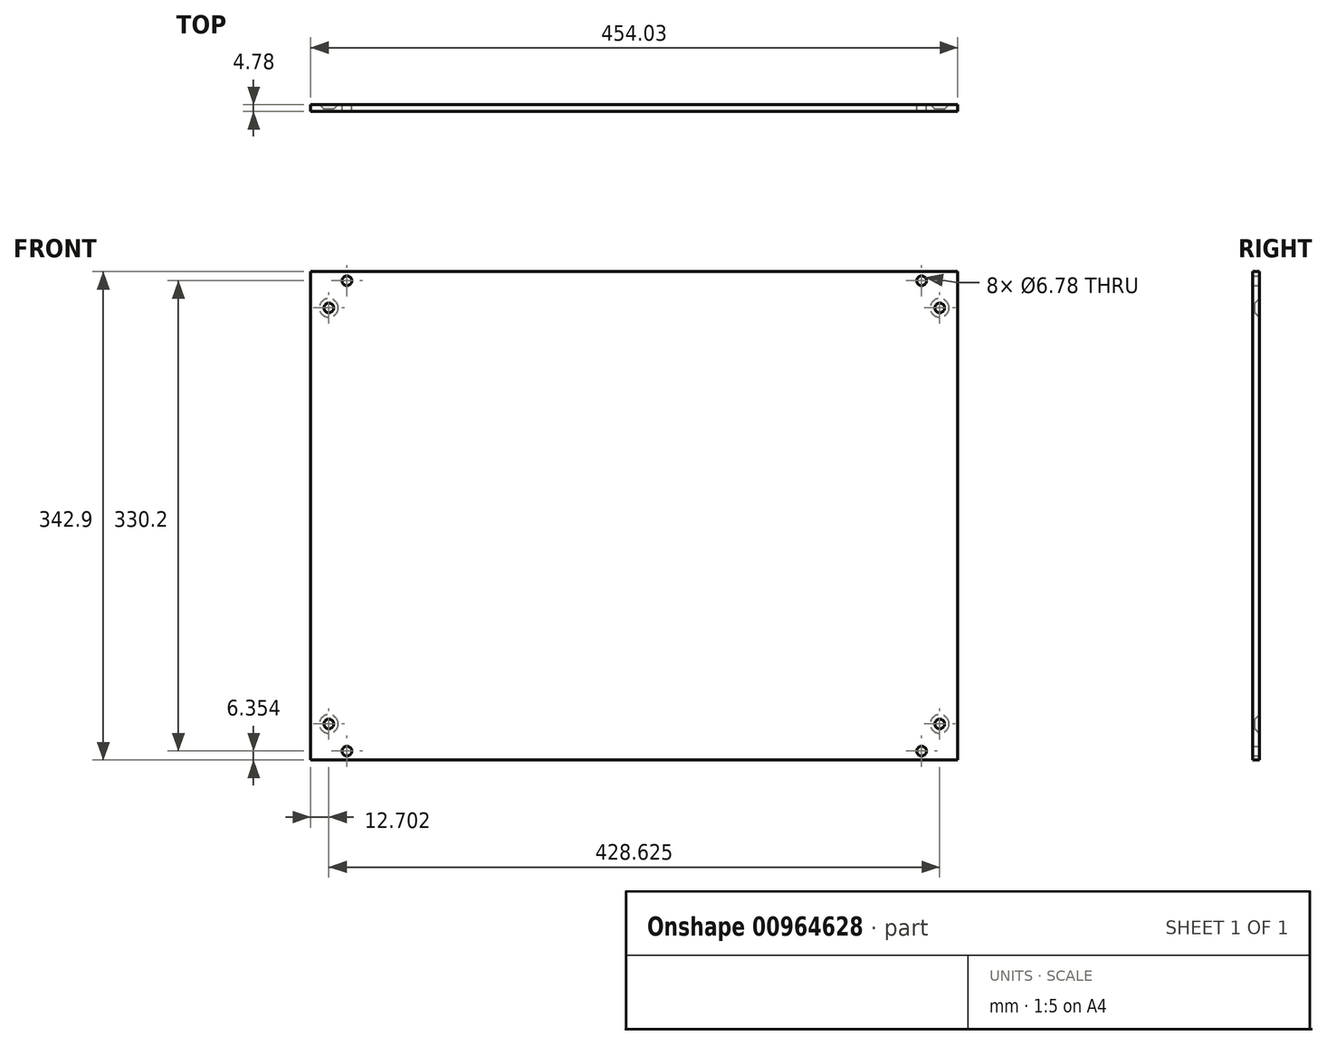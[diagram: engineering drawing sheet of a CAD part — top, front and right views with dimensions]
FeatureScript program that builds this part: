
annotation { "Feature Type Name" : "Feature", "Feature Type Description" : "" }
export const myFeature = defineFeature(function(context is Context, id is Id, definition is map)
    precondition{}
    {
        {
            var Q0;
            Q0=qCreatedBy(makeId("Front.planeOp"),FACE);
            var sketch = newSketch(context, id + "F0", { "sketchPlane" : qUnion([Q0])});
            skLineSegment(sketch, "E0.bottom", {"start": v(-161.53, 255.01) * mm, "end": v(292.5, 255.01) * mm});
            skLineSegment(sketch, "E0.top", {"start": v(-161.53, -87.89) * mm, "end": v(292.5, -87.89) * mm});
            skLineSegment(sketch, "E0.left", {"start": v(-161.53, 255.01) * mm, "end": v(-161.53, -87.89) * mm});
            skLineSegment(sketch, "E0.right", {"start": v(292.5, 255.01) * mm, "end": v(292.5, -87.89) * mm});
            skLineSegment(sketch, "E1.bottom", {"start": v(-136.13, 248.66) * mm, "end": v(267.1, 248.66) * mm, "construction": true});
            skLineSegment(sketch, "E1.top", {"start": v(-136.13, -81.54) * mm, "end": v(267.1, -81.54) * mm, "construction": true});
            skLineSegment(sketch, "E1.left", {"start": v(-136.13, 248.66) * mm, "end": v(-136.13, -81.54) * mm, "construction": true});
            skLineSegment(sketch, "E1.right", {"start": v(267.1, 248.66) * mm, "end": v(267.1, -81.54) * mm, "construction": true});
            skCircle(sketch, "E2", {"center": v(-136.13, 248.66) * mm, "radius": 3.4 * mm});
            skCircle(sketch, "E3", {"center": v(267.1, 248.66) * mm, "radius": 3.4 * mm});
            skCircle(sketch, "E4", {"center": v(-136.13, -81.54) * mm, "radius": 3.4 * mm});
            skCircle(sketch, "E5", {"center": v(-148.83, -62.49) * mm, "radius": 3.4 * mm});
            skCircle(sketch, "E6", {"center": v(-148.83, 229.61) * mm, "radius": 3.4 * mm});
            skCircle(sketch, "E7", {"center": v(279.8, 229.61) * mm, "radius": 3.4 * mm});
            skCircle(sketch, "E8", {"center": v(279.8, -62.49) * mm, "radius": 3.4 * mm});
            skLineSegment(sketch, "E9.bottom", {"start": v(-148.83, 229.61) * mm, "end": v(279.8, 229.61) * mm, "construction": true});
            skLineSegment(sketch, "E9.top", {"start": v(-148.83, -62.49) * mm, "end": v(279.8, -62.49) * mm, "construction": true});
            skLineSegment(sketch, "E9.left", {"start": v(-148.83, 229.61) * mm, "end": v(-148.83, -62.49) * mm, "construction": true});
            skLineSegment(sketch, "E9.right", {"start": v(279.8, 229.61) * mm, "end": v(279.8, -62.49) * mm, "construction": true});
            skCircle(sketch, "E10", {"center": v(267.1, -81.54) * mm, "radius": 3.4 * mm});
            skSolve(sketch);
        }
        {
            var Q0;
            Q0=makeQuery(id+"F0.imprint","IMPRINT",FACE,{"disambiguationData":[TD([[makeQuery(id+"F0.imprint","IMPRINT",EDGE,{"derivedFrom":sQuery(id+"F0.wireOp",EDGE,"E0.bottom")}),-1.0]])]});
            extrude(context, id + "F1", {"entities" : qUnion([Q0]), "depth" : 4.78 * mm, "offsetDistance" : 25.4 * mm});
        }
        {
            var Q0;
            Q0=makeQuery(id+"F1.opExtrude","CAP_EDGE",EDGE,{"disambiguationData":[OSD([sQuery(id+"F0.wireOp",EDGE,"E5")])],"isStart":true});
            var Q1;
            Q1=makeQuery(id+"F1.opExtrude","CAP_EDGE",EDGE,{"disambiguationData":[OSD([sQuery(id+"F0.wireOp",EDGE,"E8")])],"isStart":true});
            var Q2;
            Q2=makeQuery(id+"F1.opExtrude","CAP_EDGE",EDGE,{"disambiguationData":[OSD([sQuery(id+"F0.wireOp",EDGE,"E7")])],"isStart":true});
            var Q3;
            Q3=makeQuery(id+"F1.opExtrude","CAP_EDGE",EDGE,{"disambiguationData":[OSD([sQuery(id+"F0.wireOp",EDGE,"E6")])],"isStart":true});
            chamfer(context, id + "F2", {"entities" : qUnion([Q0, Q1, Q2, Q3]), "width" : 3.17 * mm, "tangentPropagation" : true});
        }
    });
